# Revit family: Sink-Undermount-Lavatory-KALLISTA-Bacifiore-P72080
name_source: partatom
category: Plumbing Fixtures
units: mm (PartAtom-declared; Revit-internal decimal feet)

## family parameters
Cut with Voids When Loaded = No
Host = Face
Maintain Annotation Orientation = No
OmniClass Number = 23.31.13.00
OmniClass Title = Sinks
Part Type = Normal
Room Calculation Point = No
Round Connector Dimension = Use Diameter
Shared = No

## types (4) — shared parameters
ADA Compliant = Yes
Assembly Code = D2010400
CW Connection = No
Cold Water Inlet = Cold Water Inlet
Date Modified = 06/25/2025
Default Elevation = 36"
Description = Under-mount sink
Drain Included = Yes
HW Connection = No
Height = 5 5/8"
Hot Water Inlet = Hot Water Inlet
Length = 19"
Manufacturer = Kallista Co.
Master Format 2014 = 22 41 16
Master Format 2014 Name = Residential Lavatories and Sinks
Material = Stainless Steel
Product Documentation Link = https://techcomm.kohler.com
Product Name = Bacifiore
Product Page URL = https://www.kallista.com
URL = https://www.kallista.com
Vent Connection = No
Waste Connection = Yes
Waste Water Outlet = Waste Water Outlet
WaterSense Certified = No
Width = 15"

## per-type parameters (varying)
| type | Finish | Model | Type |
| CDS-Distressed Silicon Charcoal | Kallista-Metal-CDS-Distressed_Silicon_Charcoal | P72080-00-CDS | 1 |
| DPC-Distressed Silicon Copper | Kallista-Metal-DPC-Distressed_Silicon_Copper | P72080-00-DPC | 2 |
| DSZ-Distressed Polished Silicon Bronze | Kallista-Metal-DSZ-Distressed_Polished_Silicon_Bronze | P72080-00-DSZ | 3 |
| PDS-Polished Distressed Steel | Kallista-Metal-PDS-Polished_Distressed_Steel | P72080-00-PDS | 4 |

## geometry (parser evidence)
native form markers: Sweep x6
no freeform markers — native parametric forms only
